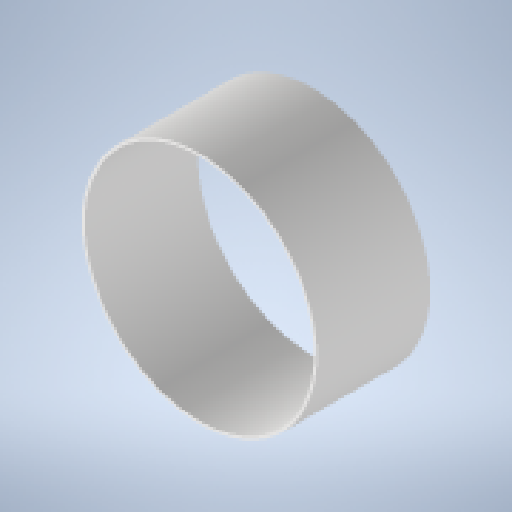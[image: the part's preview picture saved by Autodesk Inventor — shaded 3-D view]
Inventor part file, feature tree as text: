
AUTODESK INVENTOR PART (.ipt)
format: ipt  version: 2023.1 (Build 271208000, 208)  size: 142,848 bytes
history: native  units: mm
features: extrude x1, sketch x1
ambient origin geometry x8: Origin, YZ Plane, XZ Plane, XY Plane, X Axis, Y Axis, Z Axis, Center Point
bodies: Solid1 (feature_tree)
feature tree (2):
  extrude  "Extrusion1"  Depth=80.0mm
  sketch  "Sketch1"  dims[d0=166.0mm d1=2.0mm d2=80.0mm d3=0.0mm]
